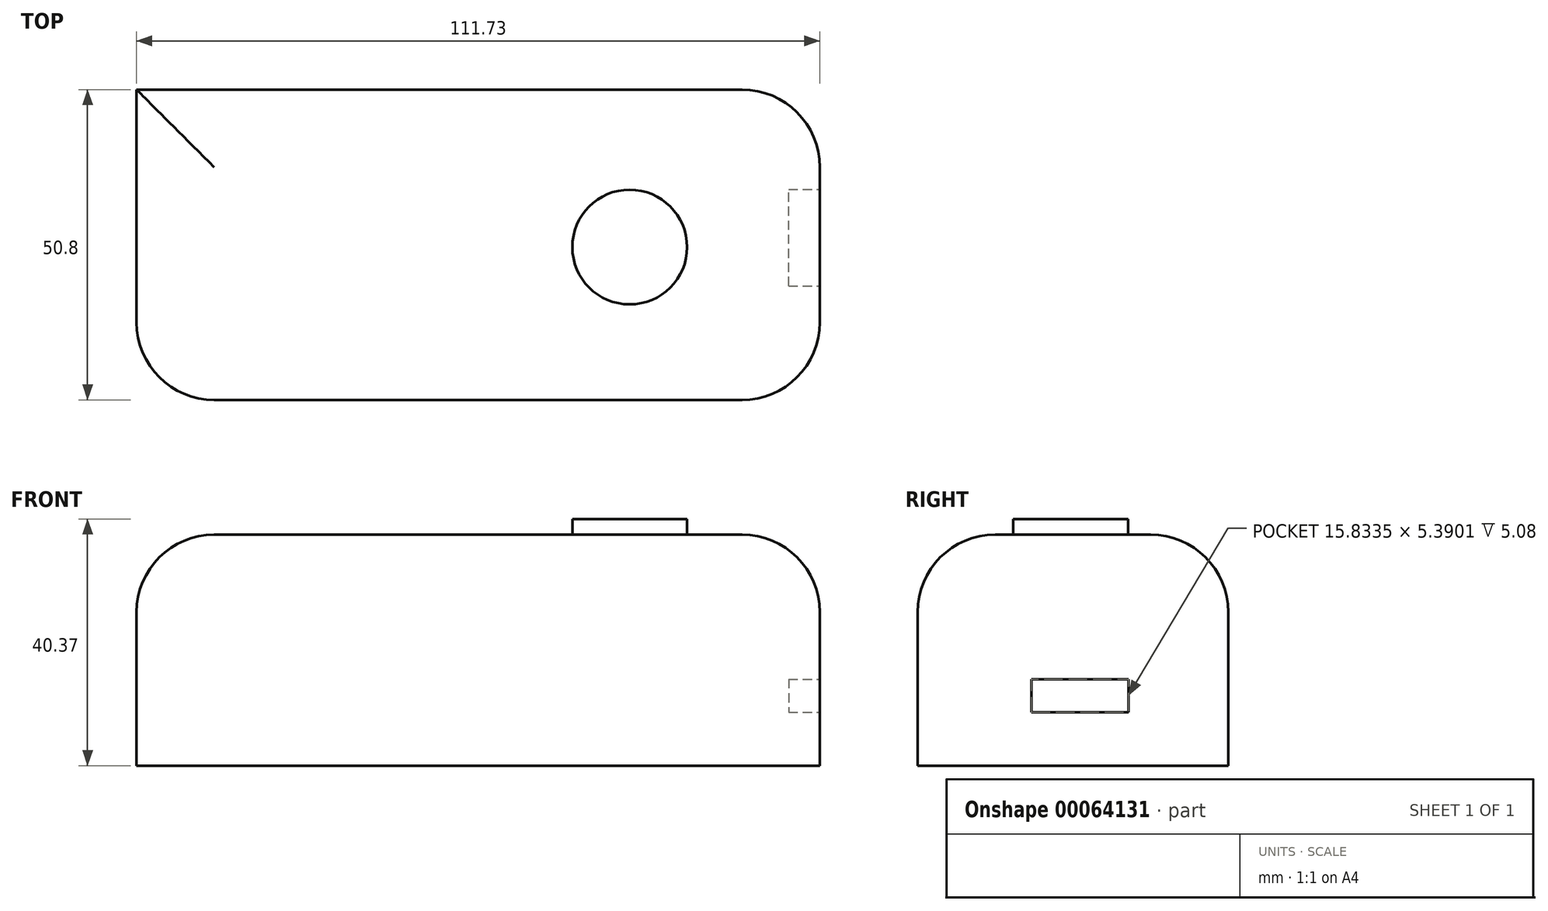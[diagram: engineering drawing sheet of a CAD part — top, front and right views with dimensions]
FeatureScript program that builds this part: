
annotation { "Feature Type Name" : "Feature", "Feature Type Description" : "" }
export const myFeature = defineFeature(function(context is Context, id is Id, definition is map)
    precondition{}
    {
        {
            var Q0;
            Q0=qCreatedBy(makeId("Front.planeOp"),FACE);
            var sketch = newSketch(context, id + "F0", { "sketchPlane" : qUnion([Q0])});
            skLineSegment(sketch, "E0.bottom", {"start": v(-52.52, 17.45) * mm, "end": v(59.2, 17.45) * mm});
            skLineSegment(sketch, "E0.top", {"start": v(-52.52, -20.38) * mm, "end": v(59.2, -20.38) * mm});
            skLineSegment(sketch, "E0.left", {"start": v(-52.52, 17.45) * mm, "end": v(-52.52, -20.38) * mm});
            skLineSegment(sketch, "E0.right", {"start": v(59.2, 17.45) * mm, "end": v(59.2, -20.38) * mm});
            skSolve(sketch);
        }
        {
            var Q0;
            Q0 = qSketchRegion(id + "F0", true);
            extrude(context, id + "F1", {"entities" : qUnion([Q0]), "depth" : 50.8 * mm});
        }
        {
            var Q0;
            Q0=makeQuery(id+"F1.opExtrude","SWEPT_FACE",FACE,{"disambiguationData":[OSD([sQuery(id+"F0.wireOp",EDGE,"E0.bottom")])]});
            fillet(context, id + "F2", {"entities" : qUnion([Q0]), "radius" : 12.7 * mm, "tangentPropagation" : true, "allowEdgeOverflow" : false});
        }
        {
            var Q0;
            Q0=makeQuery(id+"F2.opFillet","BLEND_FACE",FACE,{"disambiguationData":[OSD([sQuery(id+"F0.wireOp",EDGE,"E0.bottom"),sQuery(id+"F0.wireOp",EDGE,"E0.right")])]});
            var Q1;
            {var subQ0=sQuery(id+"F0.wireOp",EDGE,"E0.bottom");Q1=makeQuery(id+"F2.opFillet","BLEND_FACE",FACE,{"disambiguationData":[OSD([subQ0]),TDD([makeQuery(id+"F1.opExtrude","CAP_EDGE",EDGE,{"disambiguationData":[OSD([subQ0])],"isStart":false})])]});}
            fillet(context, id + "F3", {"entities" : qUnion([Q0, Q1]), "radius" : 12.7 * mm, "tangentPropagation" : true, "allowEdgeOverflow" : false});
        }
        {
            var Q0;
            Q0=makeQuery(id+"F1.opExtrude","SWEPT_FACE",FACE,{"disambiguationData":[OSD([sQuery(id+"F0.wireOp",EDGE,"E0.right")])]});
            var sketch = newSketch(context, id + "F4", { "sketchPlane" : qUnion([Q0])});
            skLineSegment(sketch, "E1.bottom", {"start": v(-32.15, -6.23) * mm, "end": v(-16.32, -6.23) * mm});
            skLineSegment(sketch, "E1.top", {"start": v(-32.15, -11.62) * mm, "end": v(-16.32, -11.62) * mm});
            skLineSegment(sketch, "E1.left", {"start": v(-32.15, -6.23) * mm, "end": v(-32.15, -11.62) * mm});
            skLineSegment(sketch, "E1.right", {"start": v(-16.32, -6.23) * mm, "end": v(-16.32, -11.62) * mm});
            skSolve(sketch);
        }
        {
            var Q0;
            Q0=makeQuery(id+"F4.imprint","IMPRINT",FACE,{"disambiguationData":[TD([[makeQuery(id+"F4.imprint","IMPRINT",EDGE,{"derivedFrom":sQuery(id+"F4.wireOp",EDGE,"E1.bottom")}),-1.0]])]});
            extrude(context, id + "F5", {"entities" : qUnion([Q0]), "operationType" : NewBodyOperationType.REMOVE, "oppositeDirection" : true, "depth" : 5.08 * mm});
        }
        {
            var Q0;
            Q0=makeQuery(id+"F1.opExtrude","SWEPT_FACE",FACE,{"disambiguationData":[OSD([sQuery(id+"F0.wireOp",EDGE,"E0.bottom")])]});
            var sketch = newSketch(context, id + "F6", { "sketchPlane" : qUnion([Q0])});
            skCircle(sketch, "E2", {"center": v(28.13, -25.77) * mm, "radius": 9.38 * mm});
            skSolve(sketch);
        }
        {
            var Q0;
            Q0 = qSketchRegion(id + "F6", true);
            extrude(context, id + "F7", {"entities" : qUnion([Q0]), "depth" : 2.54 * mm});
        }
    });
